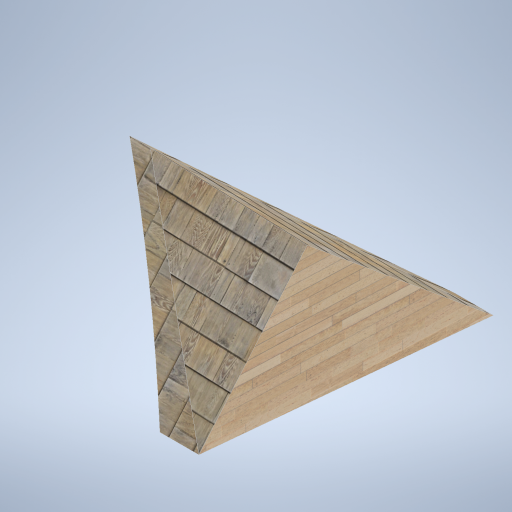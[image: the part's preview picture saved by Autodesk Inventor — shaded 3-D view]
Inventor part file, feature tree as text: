
AUTODESK INVENTOR PART (.ipt)
format: ipt  version: 2024.2 (Build 282272000, 272)  size: 404,992 bytes
history: native  units: in
note: dims shown in document units (in); Inventor stores cm internally (conversion verified against a paired STEP export)
features: sketch x6, plane x5, other x3
ambient origin geometry x8: Origin, YZ Plane, XZ Plane, XY Plane, X Axis, Y Axis, Z Axis, Center Point
bodies: Solid1 (feature_tree)
feature tree (14):
  other  "panel_pad_03.ipt"
  other  "Solid1::panel_pad_03.ipt"
  other  "TaggingFeature1"
  sketch  "Sketch1"  dims[d0=0.3937in]
  sketch  "Sketch2"
  sketch  "Sketch3"
  sketch  "Sketch6"
  sketch  "Sketch7"
  sketch  "Sketch8"
  plane  "Work Plane1"
  plane  "Work Plane2"
  plane  "Work Plane3"
  plane  "Work Plane4"
  plane  "Work Plane5"
